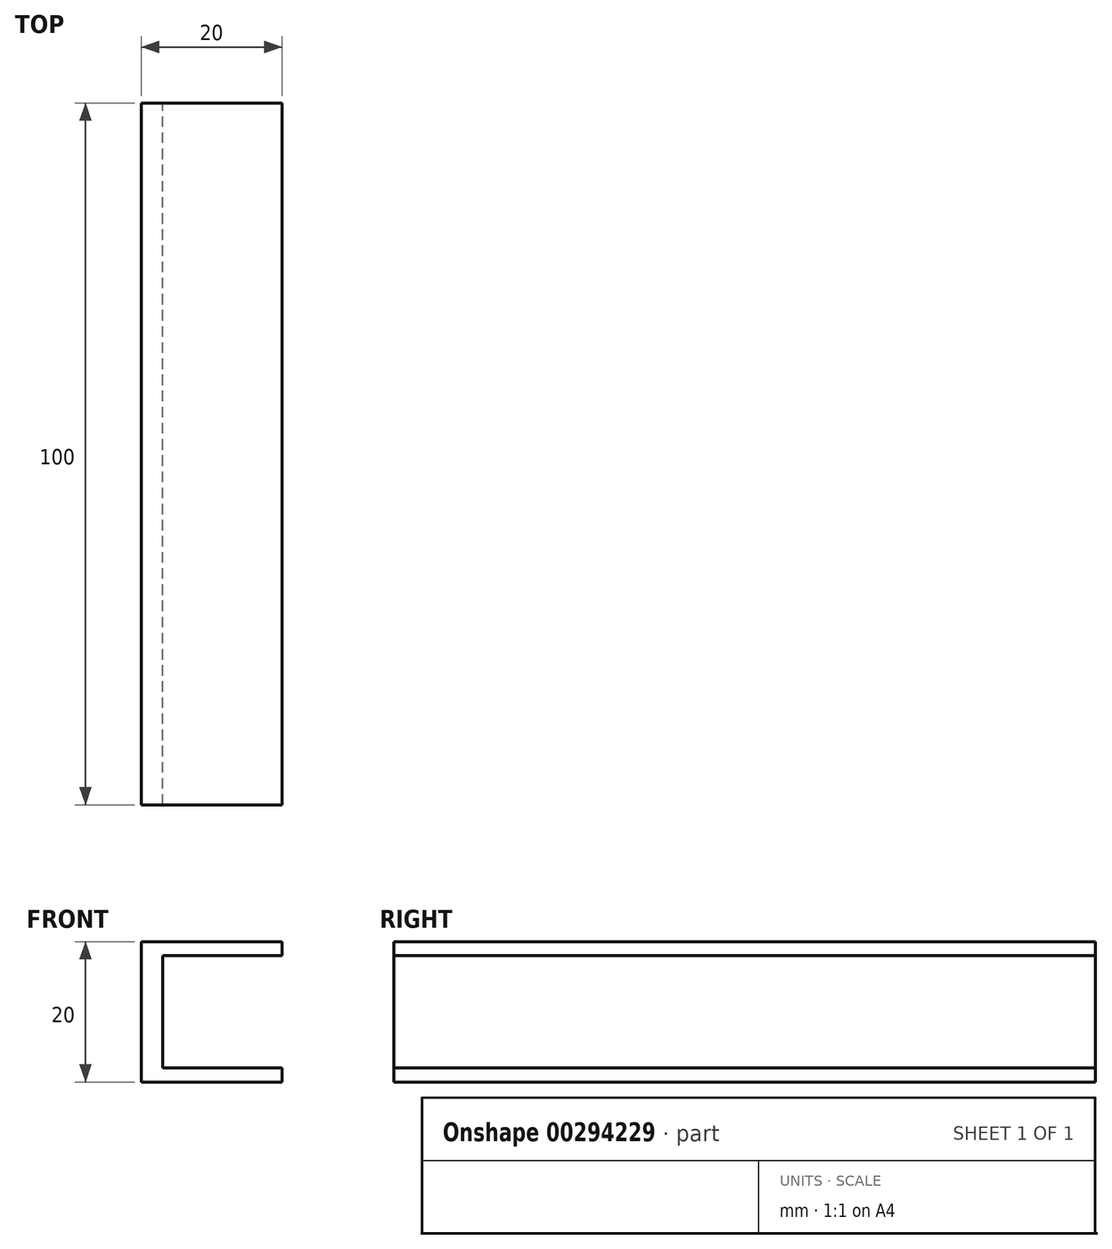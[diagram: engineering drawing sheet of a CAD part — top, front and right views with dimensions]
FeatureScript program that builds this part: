
annotation { "Feature Type Name" : "Feature", "Feature Type Description" : "" }
export const myFeature = defineFeature(function(context is Context, id is Id, definition is map)
    precondition{}
    {
        {
            var Q0;
            Q0=qCreatedBy(makeId("Front.planeOp"),FACE);
            var sketch = newSketch(context, id + "F0", { "sketchPlane" : qUnion([Q0])});
            skLineSegment(sketch, "E0.bottom", {"start": v(-10, 10) * mm, "end": v(10, 10) * mm});
            skLineSegment(sketch, "E0.top", {"start": v(-10, -10) * mm, "end": v(10, -10) * mm});
            skLineSegment(sketch, "E0.left", {"start": v(-10, 10) * mm, "end": v(-10, -10) * mm});
            skLineSegment(sketch, "E0.right", {"start": v(10, 10) * mm, "end": v(10, 8) * mm});
            skPoint(sketch, "E0.middle", {"position": v(0, 0) * mm});
            skLineSegment(sketch, "E1", {"start": v(10, 8) * mm, "end": v(-7, 8) * mm});
            skLineSegment(sketch, "E2", {"start": v(-7, 8) * mm, "end": v(-7, -8) * mm});
            skLineSegment(sketch, "E3", {"start": v(-7, -8) * mm, "end": v(10, -8) * mm});
            skLineSegment(sketch, "E4.trimOffspring", {"start": v(10, -8) * mm, "end": v(10, -10) * mm});
            skSolve(sketch);
        }
        {
            var Q0;
            Q0 = qSketchRegion(id + "F0", true);
            extrude(context, id + "F1", {"entities" : qUnion([Q0]), "depth" : 100 * mm});
        }
    });
